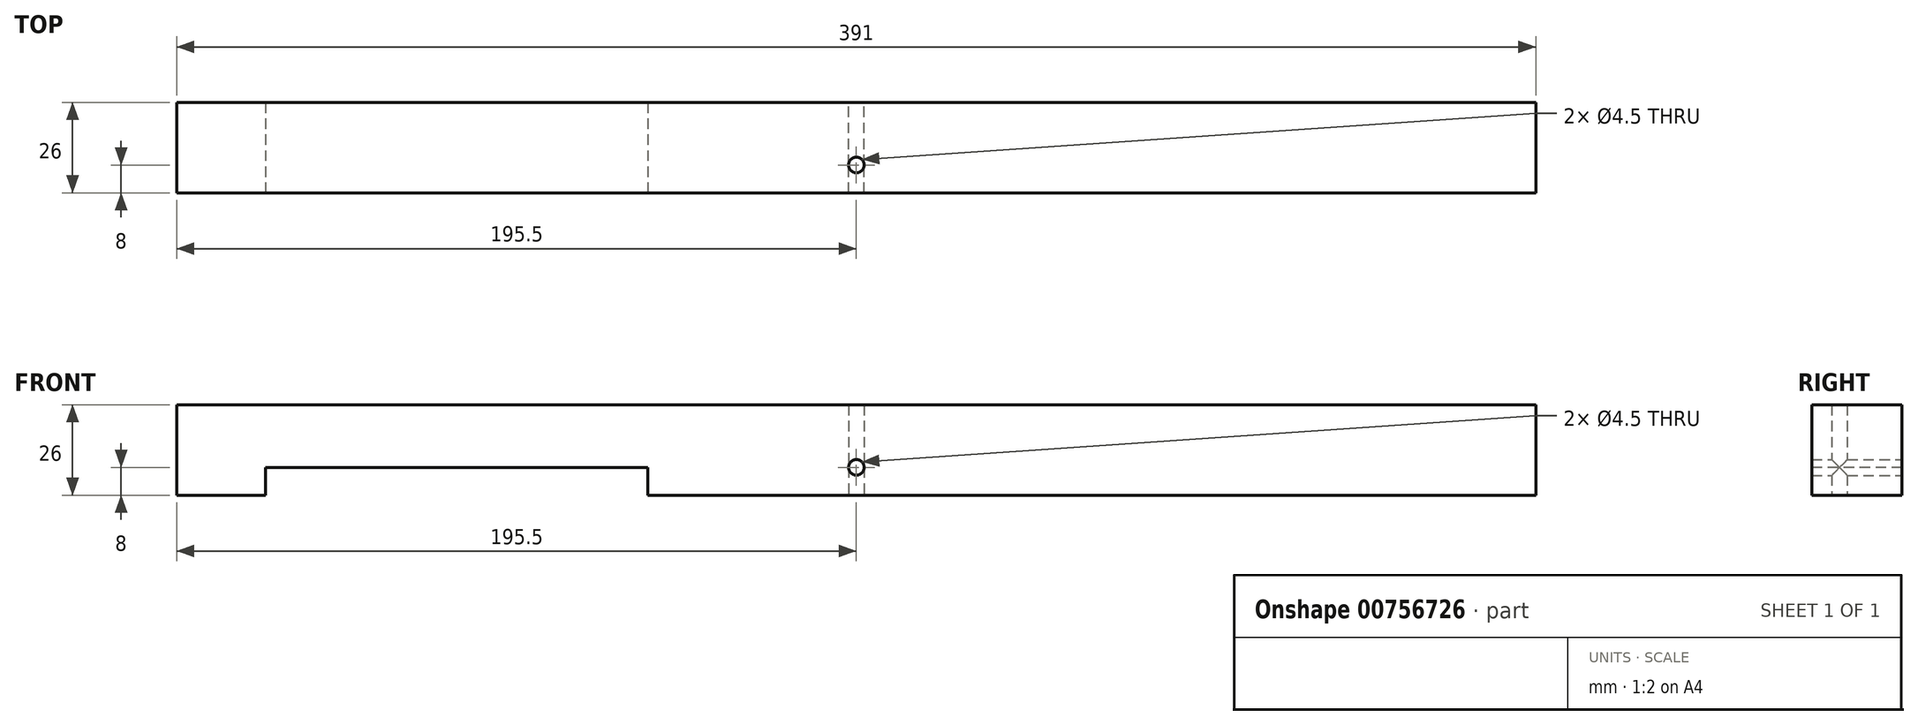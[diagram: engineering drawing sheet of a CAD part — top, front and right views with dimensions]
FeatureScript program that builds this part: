
annotation { "Feature Type Name" : "Feature", "Feature Type Description" : "" }
export const myFeature = defineFeature(function(context is Context, id is Id, definition is map)
    precondition{}
    {
        {
            var Q0;
            Q0=qCreatedBy(makeId("Right.planeOp"),FACE);
            var sketch = newSketch(context, id + "F0", { "sketchPlane" : qUnion([Q0])});
            skLineSegment(sketch, "E0.bottom", {"start": v(-13, 26) * mm, "end": v(13, 26) * mm});
            skLineSegment(sketch, "E0.top", {"start": v(-13, 0) * mm, "end": v(13, 0) * mm});
            skLineSegment(sketch, "E0.left", {"start": v(-13, 26) * mm, "end": v(-13, 0) * mm});
            skLineSegment(sketch, "E0.right", {"start": v(13, 26) * mm, "end": v(13, 0) * mm});
            skSolve(sketch);
        }
        {
            var Q0;
            Q0=makeQuery(id+"F0.imprint","IMPRINT",FACE,{"disambiguationData":[TD([[makeQuery(id+"F0.imprint","IMPRINT",EDGE,{"derivedFrom":sQuery(id+"F0.wireOp",EDGE,"E0.bottom")}),-1.0]])]});
            extrude(context, id + "F1", {"entities" : qUnion([Q0]), "depth" : 391 * mm, "offsetDistance" : 25 * mm, "symmetric" : true});
        }
        {
            var Q0;
            Q0=makeQuery(id+"F1.opExtrude","SWEPT_FACE",FACE,{"disambiguationData":[OSD([sQuery(id+"F0.wireOp",EDGE,"E0.bottom")])]});
            var sketch = newSketch(context, id + "F2", { "sketchPlane" : qUnion([Q0])});
            skLineSegment(sketch, "E1.bottom", {"start": v(-6, 13) * mm, "end": v(6, 13) * mm});
            skLineSegment(sketch, "E1.top", {"start": v(-6, 8) * mm, "end": v(6, 8) * mm});
            skLineSegment(sketch, "E1.left", {"start": v(-6, 13) * mm, "end": v(-6, 8) * mm});
            skLineSegment(sketch, "E1.right", {"start": v(6, 13) * mm, "end": v(6, 8) * mm});
            skSolve(sketch);
        }
        {
            var Q0;
            Q0=makeQuery(id+"F1.opExtrude","SWEPT_FACE",FACE,{"disambiguationData":[OSD([sQuery(id+"F0.wireOp",EDGE,"E0.left")])]});
            var sketch = newSketch(context, id + "F3", { "sketchPlane" : qUnion([Q0])});
            skLineSegment(sketch, "E2.bottom", {"start": v(-170, 8) * mm, "end": v(-60, 8) * mm});
            skLineSegment(sketch, "E2.top", {"start": v(-170, 0) * mm, "end": v(-60, 0) * mm});
            skLineSegment(sketch, "E2.left", {"start": v(-170, 8) * mm, "end": v(-170, 0) * mm});
            skLineSegment(sketch, "E2.right", {"start": v(-60, 8) * mm, "end": v(-60, 0) * mm});
            skSolve(sketch);
        }
        {
            var Q0;
            Q0=makeQuery(id+"F3.imprint","IMPRINT",FACE,{"disambiguationData":[TD([[makeQuery(id+"F3.imprint","IMPRINT",EDGE,{"derivedFrom":sQuery(id+"F3.wireOp",EDGE,"E2.bottom")}),-1.0]])]});
            extrude(context, id + "F4", {"entities" : qUnion([Q0]), "operationType" : NewBodyOperationType.REMOVE, "endBound" : BoundingType.UP_TO_NEXT, "oppositeDirection" : true, "depth" : 25 * mm, "offsetDistance" : 25 * mm});
        }
        {
            var Q0;
            Q0=makeQuery(id+"F1.opExtrude","SWEPT_FACE",FACE,{"disambiguationData":[OSD([sQuery(id+"F0.wireOp",EDGE,"E0.left")])]});
            var sketch = newSketch(context, id + "F5", { "sketchPlane" : qUnion([Q0])});
            skPoint(sketch, "E3", {"position": v(0, 8) * mm});
            skSolve(sketch);
        }
        {
            var Q0;
            Q0=sQuery(id+"F5.wireOp",VERTEX,"E3");
            var Q1;
            Q1=makeQuery(id+"F1.opExtrude","SWEPT_BODY",BODY,{"disambiguationData":[OSD([sQuery(id+"F0.wireOp",EDGE,"E0.bottom"),sQuery(id+"F0.wireOp",EDGE,"E0.top"),sQuery(id+"F0.wireOp",EDGE,"E0.left"),sQuery(id+"F0.wireOp",EDGE,"E0.right")])]});
            hole(context, id + "F6", {"style" : HoleStyle.SIMPLE, "endStyle" : HoleEndStyle.THROUGH, "holeDiameter" : 4.5 * mm, "majorDiameter" : 5 * mm, "isTappedThrough" : true, "tappedDepth" : 12 * mm, "tapClearance" : 3, "locations" : qUnion([Q0]), "scope" : qUnion([Q1])});
        }
        {
            var Q0;
            Q0=makeQuery(id+"F2.imprint","IMPRINT",FACE,{"disambiguationData":[TD([[makeQuery(id+"F2.imprint","IMPRINT",EDGE,{"derivedFrom":sQuery(id+"F2.wireOp",EDGE,"E1.top")}),-1.0]])]});
            var sketch = newSketch(context, id + "F7", { "sketchPlane" : qUnion([Q0])});
            skPoint(sketch, "E4", {"position": v(0, -5) * mm});
            skSolve(sketch);
        }
        {
            var Q0;
            Q0=sQuery(id+"F7.wireOp",VERTEX,"E4");
            var Q1;
            Q1=makeQuery(id+"F1.opExtrude","SWEPT_BODY",BODY,{"disambiguationData":[OSD([sQuery(id+"F0.wireOp",EDGE,"E0.bottom"),sQuery(id+"F0.wireOp",EDGE,"E0.top"),sQuery(id+"F0.wireOp",EDGE,"E0.left"),sQuery(id+"F0.wireOp",EDGE,"E0.right")])]});
            hole(context, id + "F8", {"style" : HoleStyle.SIMPLE, "endStyle" : HoleEndStyle.THROUGH, "holeDiameter" : 4.5 * mm, "majorDiameter" : 5 * mm, "isTappedThrough" : true, "tappedDepth" : 12 * mm, "tapClearance" : 3, "locations" : qUnion([Q0]), "scope" : qUnion([Q1])});
        }
    });
